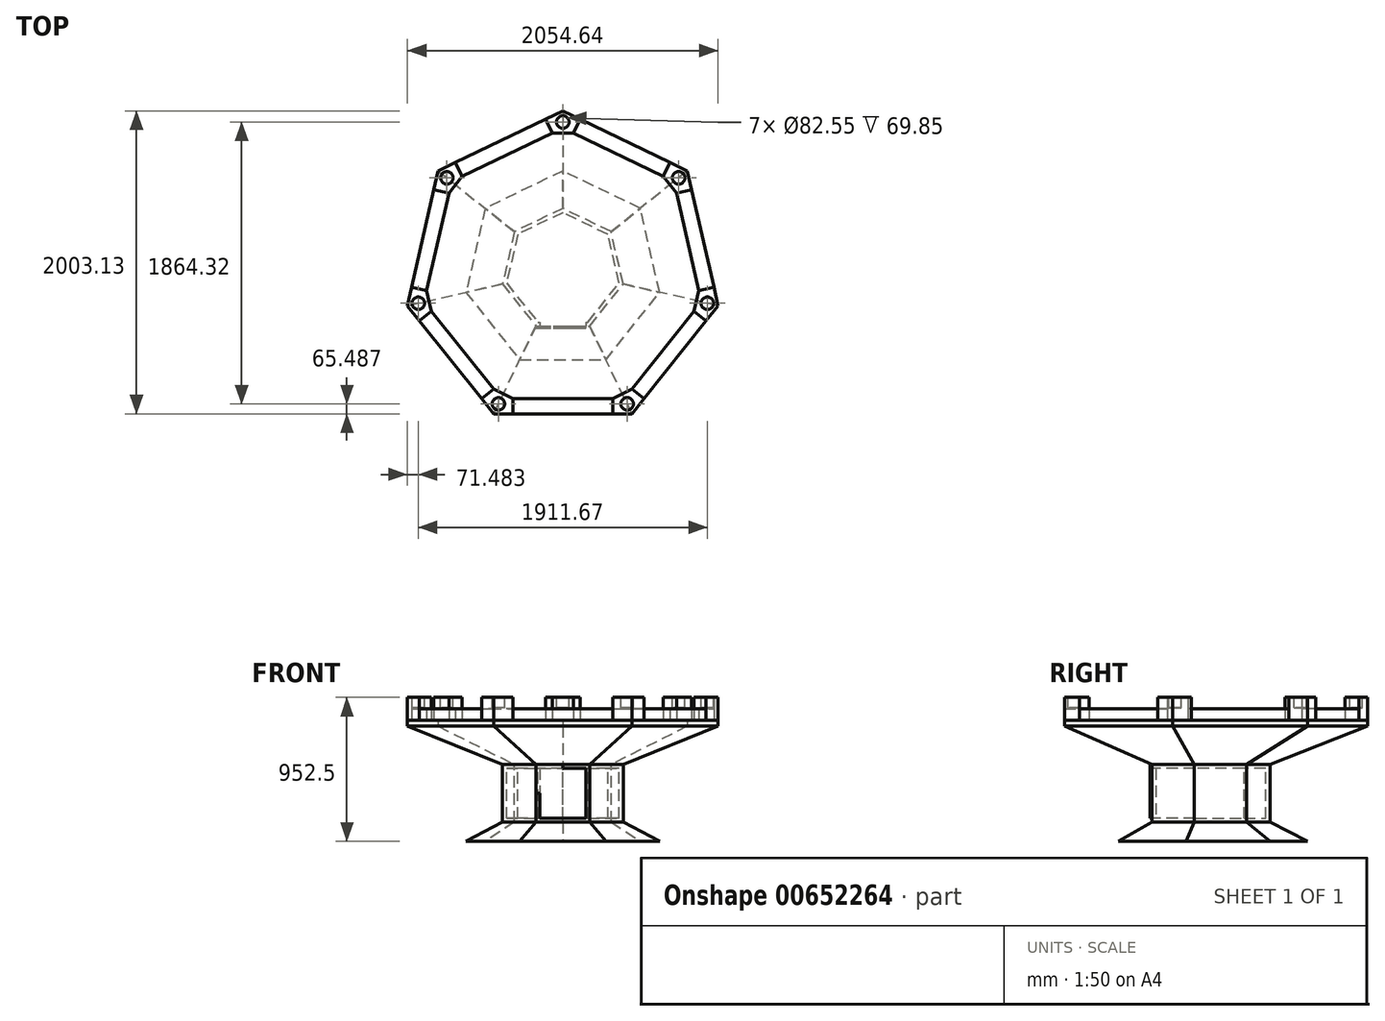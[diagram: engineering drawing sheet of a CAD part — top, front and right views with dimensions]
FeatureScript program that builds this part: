
annotation { "Feature Type Name" : "Feature", "Feature Type Description" : "" }
export const myFeature = defineFeature(function(context is Context, id is Id, definition is map)
    precondition{}
    {
        {
            var Q0;
            Q0=qCreatedBy(makeId("Top.planeOp"),FACE);
            var sketch = newSketch(context, id + "F0", { "sketchPlane" : qUnion([Q0])});
            skCircle(sketch, "E0.cCircle", {"center": v(0, 0) * mm, "radius": 949.39 * mm, "construction": true});
            skLineSegment(sketch, "E0.0", {"start": v(457.2, -949.39) * mm, "end": v(-457.2, -949.39) * mm});
            skLineSegment(sketch, "E0.1", {"start": v(-457.2, -949.39) * mm, "end": v(-1027.32, -234.48) * mm});
            skLineSegment(sketch, "E0.2", {"start": v(-1027.32, -234.48) * mm, "end": v(-823.85, 657) * mm});
            skLineSegment(sketch, "E0.3", {"start": v(-823.85, 657) * mm, "end": v(0, 1053.74) * mm});
            skLineSegment(sketch, "E0.4", {"start": v(0, 1053.74) * mm, "end": v(823.85, 657) * mm});
            skLineSegment(sketch, "E0.5", {"start": v(823.85, 657) * mm, "end": v(1027.32, -234.48) * mm});
            skLineSegment(sketch, "E0.6", {"start": v(1027.32, -234.48) * mm, "end": v(457.2, -949.39) * mm});
            skPoint(sketch, "E0.0.midPoint", {"position": v(0, -949.39) * mm});
            skSolve(sketch);
        }
        {
            var Q0;
            Q0 = qSketchRegion(id + "F0", true);
            extrude(context, id + "F1", {"entities" : qUnion([Q0]), "depth" : 38.1 * mm, "offsetDistance" : 25.4 * mm});
        }
        {
            var Q0;
            Q0=qCreatedBy(makeId("Front.planeOp"),FACE);
            var sketch = newSketch(context, id + "F2", { "sketchPlane" : qUnion([Q0])});
            skLineSegment(sketch, "E1.bottom", {"start": v(-2163.19, 801.55) * mm, "end": v(-1858.39, 801.55) * mm});
            skLineSegment(sketch, "E1.top", {"start": v(-2163.19, -1027.25) * mm, "end": v(-1858.39, -1027.25) * mm});
            skLineSegment(sketch, "E1.left", {"start": v(-2163.19, 801.55) * mm, "end": v(-2163.19, -1027.25) * mm});
            skLineSegment(sketch, "E1.right", {"start": v(-1858.39, 801.55) * mm, "end": v(-1858.39, -1027.25) * mm});
            skSolve(sketch);
        }
        {
            var Q0;
            Q0=makeQuery(id+"F1.opExtrude","CAP_FACE",FACE,{"disambiguationData":[OSD([sQuery(id+"F0.wireOp",EDGE,"E0.0"),sQuery(id+"F0.wireOp",EDGE,"E0.1"),sQuery(id+"F0.wireOp",EDGE,"E0.2"),sQuery(id+"F0.wireOp",EDGE,"E0.3"),sQuery(id+"F0.wireOp",EDGE,"E0.4"),sQuery(id+"F0.wireOp",EDGE,"E0.5"),sQuery(id+"F0.wireOp",EDGE,"E0.6")])],"isStart":false});
            var sketch = newSketch(context, id + "F3", { "sketchPlane" : qUnion([Q0])});
            skLineSegment(sketch, "E2", {"start": v(330.2, -949.39) * mm, "end": v(330.2, -847.79) * mm});
            skLineSegment(sketch, "E3", {"start": v(457.2, -949.39) * mm, "end": v(330.2, -949.39) * mm});
            skLineSegment(sketch, "E4", {"start": v(457.2, -949.39) * mm, "end": v(536.38, -850.1) * mm});
            skLineSegment(sketch, "E5", {"start": v(536.38, -850.1) * mm, "end": v(456.95, -786.75) * mm});
            skLineSegment(sketch, "E6", {"start": v(456.95, -786.75) * mm, "end": v(330.2, -847.79) * mm});
            skLineSegment(sketch, "E7", {"start": v(457.2, -949.39) * mm, "end": v(393.57, -817.27) * mm});
            skLineSegment(sketch, "E8", {"start": v(-457.2, -949.39) * mm, "end": v(-330.2, -949.39) * mm});
            skLineSegment(sketch, "E9", {"start": v(-457.2, -949.39) * mm, "end": v(-536.38, -850.1) * mm});
            skLineSegment(sketch, "E10", {"start": v(-536.38, -850.1) * mm, "end": v(-456.95, -786.75) * mm});
            skLineSegment(sketch, "E11", {"start": v(-330.2, -949.39) * mm, "end": v(-330.2, -847.79) * mm});
            skLineSegment(sketch, "E12", {"start": v(-456.95, -786.75) * mm, "end": v(-330.2, -847.79) * mm});
            skLineSegment(sketch, "E13", {"start": v(-457.2, -949.39) * mm, "end": v(-393.57, -817.27) * mm});
            skLineSegment(sketch, "E14", {"start": v(1027.32, -234.48) * mm, "end": v(948.14, -333.77) * mm});
            skLineSegment(sketch, "E15", {"start": v(1027.32, -234.48) * mm, "end": v(999.06, -110.66) * mm});
            skLineSegment(sketch, "E16", {"start": v(948.14, -333.77) * mm, "end": v(868.7, -270.42) * mm});
            skLineSegment(sketch, "E17", {"start": v(999.06, -110.66) * mm, "end": v(900, -133.27) * mm});
            skLineSegment(sketch, "E18", {"start": v(900, -133.27) * mm, "end": v(868.7, -270.42) * mm});
            skLineSegment(sketch, "E19", {"start": v(1027.32, -234.48) * mm, "end": v(884.35, -201.85) * mm});
            skLineSegment(sketch, "E20", {"start": v(-1027.32, -234.48) * mm, "end": v(-999.06, -110.66) * mm});
            skLineSegment(sketch, "E21", {"start": v(-1027.32, -234.48) * mm, "end": v(-948.14, -333.77) * mm});
            skLineSegment(sketch, "E22", {"start": v(-999.06, -110.66) * mm, "end": v(-900, -133.27) * mm});
            skLineSegment(sketch, "E23", {"start": v(-948.14, -333.77) * mm, "end": v(-868.7, -270.42) * mm});
            skLineSegment(sketch, "E24", {"start": v(-900, -133.27) * mm, "end": v(-868.7, -270.42) * mm});
            skLineSegment(sketch, "E25", {"start": v(-1027.32, -234.48) * mm, "end": v(-884.35, -201.85) * mm});
            skLineSegment(sketch, "E26", {"start": v(-823.85, 657) * mm, "end": v(-852.1, 533.18) * mm});
            skLineSegment(sketch, "E27", {"start": v(-823.85, 657) * mm, "end": v(-709.42, 712.1) * mm});
            skLineSegment(sketch, "E28", {"start": v(-709.42, 712.1) * mm, "end": v(-665.34, 620.56) * mm});
            skLineSegment(sketch, "E29", {"start": v(-852.1, 533.18) * mm, "end": v(-753.05, 510.57) * mm});
            skLineSegment(sketch, "E30", {"start": v(-753.05, 510.57) * mm, "end": v(-665.34, 620.56) * mm});
            skLineSegment(sketch, "E31", {"start": v(-823.85, 657) * mm, "end": v(-709.2, 565.57) * mm});
            skLineSegment(sketch, "E32", {"start": v(823.85, 657) * mm, "end": v(709.42, 712.1) * mm});
            skLineSegment(sketch, "E33", {"start": v(823.85, 657) * mm, "end": v(852.1, 533.18) * mm});
            skLineSegment(sketch, "E34", {"start": v(709.42, 712.1) * mm, "end": v(665.34, 620.56) * mm});
            skLineSegment(sketch, "E35", {"start": v(852.1, 533.18) * mm, "end": v(753.05, 510.57) * mm});
            skLineSegment(sketch, "E36", {"start": v(753.05, 510.57) * mm, "end": v(665.34, 620.56) * mm});
            skLineSegment(sketch, "E37", {"start": v(823.85, 657) * mm, "end": v(709.2, 565.57) * mm});
            skLineSegment(sketch, "E38", {"start": v(0, 1053.74) * mm, "end": v(-114.42, 998.64) * mm});
            skLineSegment(sketch, "E39", {"start": v(-114.42, 998.64) * mm, "end": v(-70.34, 907.1) * mm});
            skLineSegment(sketch, "E40", {"start": v(0, 1053.74) * mm, "end": v(114.42, 998.64) * mm});
            skLineSegment(sketch, "E41", {"start": v(114.42, 998.64) * mm, "end": v(70.34, 907.1) * mm});
            skLineSegment(sketch, "E42", {"start": v(70.34, 907.1) * mm, "end": v(-70.34, 907.1) * mm});
            skLineSegment(sketch, "E43", {"start": v(0, 1053.74) * mm, "end": v(0, 907.1) * mm});
            skLineSegment(sketch, "E44", {"start": v(-330.2, -847.79) * mm, "end": v(330.2, -847.79) * mm});
            skLineSegment(sketch, "E45", {"start": v(-330.2, -949.39) * mm, "end": v(330.2, -949.39) * mm});
            skLineSegment(sketch, "E46", {"start": v(868.7, -270.42) * mm, "end": v(456.95, -786.75) * mm});
            skLineSegment(sketch, "E47", {"start": v(948.14, -333.77) * mm, "end": v(536.38, -850.1) * mm});
            skLineSegment(sketch, "E48", {"start": v(852.1, 533.18) * mm, "end": v(999.06, -110.66) * mm});
            skLineSegment(sketch, "E49", {"start": v(753.05, 510.57) * mm, "end": v(900, -133.27) * mm});
            skLineSegment(sketch, "E50", {"start": v(114.42, 998.64) * mm, "end": v(709.42, 712.1) * mm});
            skLineSegment(sketch, "E51", {"start": v(70.34, 907.1) * mm, "end": v(665.34, 620.56) * mm});
            skLineSegment(sketch, "E52", {"start": v(-114.42, 998.64) * mm, "end": v(-709.42, 712.1) * mm});
            skLineSegment(sketch, "E53", {"start": v(-70.34, 907.1) * mm, "end": v(-665.34, 620.56) * mm});
            skLineSegment(sketch, "E54", {"start": v(-753.05, 510.57) * mm, "end": v(-900, -133.27) * mm});
            skLineSegment(sketch, "E55", {"start": v(-852.1, 533.18) * mm, "end": v(-999.06, -110.66) * mm});
            skLineSegment(sketch, "E56", {"start": v(-868.7, -270.42) * mm, "end": v(-456.95, -786.75) * mm});
            skLineSegment(sketch, "E57", {"start": v(-948.14, -333.77) * mm, "end": v(-536.38, -850.1) * mm});
            skLineSegment(sketch, "E58", {"start": v(-709.2, 565.57) * mm, "end": v(709.2, 565.57) * mm});
            skLineSegment(sketch, "E59", {"start": v(-393.57, -817.27) * mm, "end": v(-709.2, 565.57) * mm});
            skLineSegment(sketch, "E60", {"start": v(393.57, -817.27) * mm, "end": v(-884.35, -201.85) * mm});
            skLineSegment(sketch, "E61", {"start": v(884.35, -201.85) * mm, "end": v(-393.57, -817.27) * mm});
            skLineSegment(sketch, "E62", {"start": v(884.35, -201.85) * mm, "end": v(0, 907.1) * mm});
            skLineSegment(sketch, "E63", {"start": v(709.2, 565.57) * mm, "end": v(393.57, -817.27) * mm});
            skLineSegment(sketch, "E64", {"start": v(-884.35, -201.85) * mm, "end": v(0, 907.1) * mm});
            skPoint(sketch, "E65", {"position": v(-612, 139.68) * mm});
            skPoint(sketch, "E66", {"position": v(-490.78, -391.38) * mm});
            skPoint(sketch, "E67", {"position": v(490.78, -391.38) * mm});
            skPoint(sketch, "E68", {"position": v(612, 139.68) * mm});
            skPoint(sketch, "E69", {"position": v(-272.36, 565.57) * mm});
            skPoint(sketch, "E70", {"position": v(272.36, 565.57) * mm});
            skPoint(sketch, "E71", {"position": v(0, -627.73) * mm});
            skLineSegment(sketch, "E72.0", {"start": v(0, -627.73) * mm, "end": v(-627.73, 0) * mm});
            skLineSegment(sketch, "E72.1", {"start": v(-627.73, 0) * mm, "end": v(0, 627.73) * mm});
            skLineSegment(sketch, "E72.2", {"start": v(0, 627.73) * mm, "end": v(627.73, 0) * mm});
            skLineSegment(sketch, "E72.3", {"start": v(627.73, 0) * mm, "end": v(0, -627.73) * mm});
            skPoint(sketch, "E73", {"position": v(-313.87, 313.87) * mm});
            skPoint(sketch, "E74", {"position": v(313.87, 313.87) * mm});
            skPoint(sketch, "E75", {"position": v(313.87, -313.87) * mm});
            skPoint(sketch, "E76", {"position": v(-313.87, -313.87) * mm});
            skLineSegment(sketch, "E77.bottom", {"start": v(-313.87, 313.87) * mm, "end": v(313.87, 313.87) * mm});
            skLineSegment(sketch, "E77.top", {"start": v(-313.87, -313.87) * mm, "end": v(313.87, -313.87) * mm});
            skLineSegment(sketch, "E77.left", {"start": v(-313.87, 313.87) * mm, "end": v(-313.87, -313.87) * mm});
            skLineSegment(sketch, "E77.right", {"start": v(313.87, 313.87) * mm, "end": v(313.87, -313.87) * mm});
            skPoint(sketch, "E78", {"position": v(-313.87, 0) * mm});
            skPoint(sketch, "E79", {"position": v(0, 313.87) * mm});
            skPoint(sketch, "E80", {"position": v(313.87, 0) * mm});
            skPoint(sketch, "E81", {"position": v(0, -313.87) * mm});
            skLineSegment(sketch, "E82", {"start": v(-313.87, 0) * mm, "end": v(-313.87, 313.87) * mm});
            skLineSegment(sketch, "E83", {"start": v(-313.87, 0) * mm, "end": v(-313.87, -313.87) * mm});
            skLineSegment(sketch, "E84", {"start": v(313.87, -313.87) * mm, "end": v(313.87, 0) * mm});
            skLineSegment(sketch, "E85", {"start": v(313.87, 0) * mm, "end": v(313.87, 313.87) * mm});
            skPoint(sketch, "E86", {"position": v(-313.87, 156.93) * mm});
            skPoint(sketch, "E87", {"position": v(-313.87, -156.93) * mm});
            skPoint(sketch, "E88", {"position": v(313.87, -156.93) * mm});
            skPoint(sketch, "E89", {"position": v(313.87, 156.93) * mm});
            skSolve(sketch);
        }
        {
            var Q0;
            {var subQ0=sQuery(id+"F3.wireOp",EDGE,"E2");Q0=makeQuery(id+"F3.imprint","IMPRINT",FACE,{"disambiguationData":[TD([[makeQuery(id+"F3.imprint","IMPRINT",EDGE,{"derivedFrom":subQ0}),-1.0]])]});}
            var Q1;
            Q1=makeQuery(id+"F3.imprint","IMPRINT",FACE,{"disambiguationData":[TD([[makeQuery(id+"F3.imprint","IMPRINT",EDGE,{"derivedFrom":sQuery(id+"F3.wireOp",EDGE,"E4")}),-1.0]])]});
            extrude(context, id + "F4", {"entities" : qUnion([Q0, Q1]), "depth" : 152.4 * mm, "offsetDistance" : 25.4 * mm});
        }
        {
            var Q0;
            Q0=makeQuery(id+"F3.imprint","IMPRINT",FACE,{"disambiguationData":[TD([[makeQuery(id+"F3.imprint","IMPRINT",EDGE,{"derivedFrom":sQuery(id+"F3.wireOp",EDGE,"E9")}),-1.0]])]});
            var Q1;
            Q1=makeQuery(id+"F3.imprint","IMPRINT",FACE,{"disambiguationData":[TD([[makeQuery(id+"F3.imprint","IMPRINT",EDGE,{"derivedFrom":sQuery(id+"F3.wireOp",EDGE,"E8")}),-1.0]])]});
            extrude(context, id + "F5", {"entities" : qUnion([Q0, Q1]), "depth" : 152.4 * mm, "offsetDistance" : 25.4 * mm});
        }
        {
            var Q0;
            Q0=makeQuery(id+"F3.imprint","IMPRINT",FACE,{"disambiguationData":[TD([[makeQuery(id+"F3.imprint","IMPRINT",EDGE,{"derivedFrom":sQuery(id+"F3.wireOp",EDGE,"E15")}),-1.0]])]});
            var Q1;
            Q1=makeQuery(id+"F3.imprint","IMPRINT",FACE,{"disambiguationData":[TD([[makeQuery(id+"F3.imprint","IMPRINT",EDGE,{"derivedFrom":sQuery(id+"F3.wireOp",EDGE,"E14")}),-1.0]])]});
            extrude(context, id + "F6", {"entities" : qUnion([Q0, Q1]), "depth" : 152.4 * mm, "offsetDistance" : 25.4 * mm});
        }
        {
            var Q0;
            Q0=makeQuery(id+"F3.imprint","IMPRINT",FACE,{"disambiguationData":[TD([[makeQuery(id+"F3.imprint","IMPRINT",EDGE,{"derivedFrom":sQuery(id+"F3.wireOp",EDGE,"E20")}),-1.0]])]});
            var Q1;
            Q1=makeQuery(id+"F3.imprint","IMPRINT",FACE,{"disambiguationData":[TD([[makeQuery(id+"F3.imprint","IMPRINT",EDGE,{"derivedFrom":sQuery(id+"F3.wireOp",EDGE,"E21")}),-1.0]])]});
            extrude(context, id + "F7", {"entities" : qUnion([Q0, Q1]), "depth" : 152.4 * mm, "offsetDistance" : 25.4 * mm});
        }
        {
            var Q0;
            Q0=makeQuery(id+"F3.imprint","IMPRINT",FACE,{"disambiguationData":[TD([[makeQuery(id+"F3.imprint","IMPRINT",EDGE,{"derivedFrom":sQuery(id+"F3.wireOp",EDGE,"E27")}),-1.0]])]});
            var Q1;
            Q1=makeQuery(id+"F3.imprint","IMPRINT",FACE,{"disambiguationData":[TD([[makeQuery(id+"F3.imprint","IMPRINT",EDGE,{"derivedFrom":sQuery(id+"F3.wireOp",EDGE,"E26")}),-1.0]])]});
            extrude(context, id + "F8", {"entities" : qUnion([Q0, Q1]), "depth" : 152.4 * mm, "offsetDistance" : 25.4 * mm});
        }
        {
            var Q0;
            Q0=makeQuery(id+"F3.imprint","IMPRINT",FACE,{"disambiguationData":[TD([[makeQuery(id+"F3.imprint","IMPRINT",EDGE,{"derivedFrom":sQuery(id+"F3.wireOp",EDGE,"E32")}),-1.0]])]});
            var Q1;
            Q1=makeQuery(id+"F3.imprint","IMPRINT",FACE,{"disambiguationData":[TD([[makeQuery(id+"F3.imprint","IMPRINT",EDGE,{"derivedFrom":sQuery(id+"F3.wireOp",EDGE,"E33")}),-1.0]])]});
            var Q2;
            Q2=sQuery(id+"F3.wireOp",EDGE,"E34");
            var Q3;
            Q3=sQuery(id+"F3.wireOp",EDGE,"E32");
            var Q4;
            Q4=sQuery(id+"F3.wireOp",EDGE,"E35");
            var Q5;
            Q5=sQuery(id+"F3.wireOp",EDGE,"E33");
            var Q6;
            Q6=sQuery(id+"F3.wireOp",EDGE,"E36");
            var Q7;
            Q7=sQuery(id+"F3.wireOp",EDGE,"E37");
            extrude(context, id + "F9", {"entities" : qUnion([Q0, Q1]), "surfaceEntities" : qUnion([Q2, Q3, Q4, Q5, Q6, Q7]), "depth" : 152.4 * mm, "offsetDistance" : 25.4 * mm});
        }
        {
            var Q0;
            Q0=makeQuery(id+"F3.imprint","IMPRINT",FACE,{"disambiguationData":[TD([[makeQuery(id+"F3.imprint","IMPRINT",EDGE,{"derivedFrom":sQuery(id+"F3.wireOp",EDGE,"E38")}),-1.0]])]});
            var Q1;
            Q1=makeQuery(id+"F3.imprint","IMPRINT",FACE,{"disambiguationData":[TD([[makeQuery(id+"F3.imprint","IMPRINT",EDGE,{"derivedFrom":sQuery(id+"F3.wireOp",EDGE,"E40")}),-1.0]])]});
            extrude(context, id + "F10", {"entities" : qUnion([Q0, Q1]), "depth" : 152.4 * mm, "offsetDistance" : 25.4 * mm});
        }
        {
            var Q0;
            Q0=makeQuery(id+"F3.imprint","IMPRINT",FACE,{"disambiguationData":[TD([[makeQuery(id+"F3.imprint","IMPRINT",EDGE,{"derivedFrom":sQuery(id+"F3.wireOp",EDGE,"E28")}),1.0]])]});
            var Q1;
            Q1=makeQuery(id+"F3.imprint","IMPRINT",FACE,{"disambiguationData":[TD([[makeQuery(id+"F3.imprint","IMPRINT",EDGE,{"derivedFrom":sQuery(id+"F3.wireOp",EDGE,"E22")}),1.0]])]});
            var Q2;
            Q2=makeQuery(id+"F3.imprint","IMPRINT",FACE,{"disambiguationData":[TD([[makeQuery(id+"F3.imprint","IMPRINT",EDGE,{"derivedFrom":sQuery(id+"F3.wireOp",EDGE,"E10")}),1.0]])]});
            var Q3;
            Q3=makeQuery(id+"F3.imprint","IMPRINT",FACE,{"disambiguationData":[TD([[makeQuery(id+"F3.imprint","IMPRINT",EDGE,{"derivedFrom":sQuery(id+"F3.wireOp",EDGE,"E2")}),1.0]])]});
            var Q4;
            Q4=makeQuery(id+"F3.imprint","IMPRINT",FACE,{"disambiguationData":[TD([[makeQuery(id+"F3.imprint","IMPRINT",EDGE,{"derivedFrom":sQuery(id+"F3.wireOp",EDGE,"E5")}),-1.0]])]});
            var Q5;
            Q5=makeQuery(id+"F3.imprint","IMPRINT",FACE,{"disambiguationData":[TD([[makeQuery(id+"F3.imprint","IMPRINT",EDGE,{"derivedFrom":sQuery(id+"F3.wireOp",EDGE,"E17")}),-1.0]])]});
            var Q6;
            Q6=makeQuery(id+"F3.imprint","IMPRINT",FACE,{"disambiguationData":[TD([[makeQuery(id+"F3.imprint","IMPRINT",EDGE,{"derivedFrom":sQuery(id+"F3.wireOp",EDGE,"E34")}),-1.0]])]});
            extrude(context, id + "F11", {"entities" : qUnion([Q0, Q1, Q2, Q3, Q4, Q5, Q6]), "depth" : 76.2 * mm, "offsetDistance" : 25.4 * mm});
        }
        {
            var Q0;
            Q0=makeQuery(id+"F1.opExtrude","CAP_FACE",FACE,{"disambiguationData":[OSD([sQuery(id+"F0.wireOp",EDGE,"E0.0"),sQuery(id+"F0.wireOp",EDGE,"E0.1"),sQuery(id+"F0.wireOp",EDGE,"E0.2"),sQuery(id+"F0.wireOp",EDGE,"E0.3"),sQuery(id+"F0.wireOp",EDGE,"E0.4"),sQuery(id+"F0.wireOp",EDGE,"E0.5"),sQuery(id+"F0.wireOp",EDGE,"E0.6")])],"isStart":true});
            var sketch = newSketch(context, id + "F12", { "sketchPlane" : qUnion([Q0])});
            skLineSegment(sketch, "E90", {"start": v(-457.2, 949.39) * mm, "end": v(-1027.32, 234.48) * mm});
            skLineSegment(sketch, "E91", {"start": v(-1027.32, 234.48) * mm, "end": v(-823.85, -657) * mm});
            skLineSegment(sketch, "E92", {"start": v(-823.85, -657) * mm, "end": v(0, -1053.74) * mm});
            skLineSegment(sketch, "E93", {"start": v(0, -1053.74) * mm, "end": v(823.85, -657) * mm});
            skLineSegment(sketch, "E94", {"start": v(823.85, -657) * mm, "end": v(1027.32, 234.48) * mm});
            skLineSegment(sketch, "E95", {"start": v(1027.32, 234.48) * mm, "end": v(457.2, 949.39) * mm});
            skLineSegment(sketch, "E96", {"start": v(457.2, 949.39) * mm, "end": v(-457.2, 949.39) * mm});
            skSolve(sketch);
        }
        {
            var Q0;
            Q0=makeQuery(id+"F12.imprint","IMPRINT",FACE,{"disambiguationData":[TD([[makeQuery(id+"F12.imprint","IMPRINT",EDGE,{"derivedFrom":sQuery(id+"F12.wireOp",EDGE,"E91")}),1.0]])]});
            cPlane(context, id + "F13", {"entities" : qUnion([Q0]), "cplaneType" : CPlaneType.OFFSET, "offset" : 254 * mm, "width" : 152.4 * mm, "height" : 152.4 * mm});
        }
        {
            var Q0;
            Q0=qCreatedBy(id+"F13.planeOp",FACE);
            var sketch = newSketch(context, id + "F14", { "sketchPlane" : qUnion([Q0])});
            skCircle(sketch, "E97.cCircle", {"center": v(0, 0) * mm, "radius": 369.06 * mm, "construction": true});
            skLineSegment(sketch, "E97.0", {"start": v(-177.73, 369.06) * mm, "end": v(177.73, 369.06) * mm});
            skLineSegment(sketch, "E97.1", {"start": v(177.73, 369.06) * mm, "end": v(399.36, 91.15) * mm});
            skLineSegment(sketch, "E97.2", {"start": v(399.36, 91.15) * mm, "end": v(320.26, -255.4) * mm});
            skLineSegment(sketch, "E97.3", {"start": v(320.26, -255.4) * mm, "end": v(0, -409.63) * mm});
            skLineSegment(sketch, "E97.4", {"start": v(0, -409.63) * mm, "end": v(-320.26, -255.4) * mm});
            skLineSegment(sketch, "E97.5", {"start": v(-320.26, -255.4) * mm, "end": v(-399.36, 91.15) * mm});
            skLineSegment(sketch, "E97.6", {"start": v(-399.36, 91.15) * mm, "end": v(-177.73, 369.06) * mm});
            skPoint(sketch, "E97.0.midPoint", {"position": v(0, 369.06) * mm});
            skSolve(sketch);
        }
        {
            var Q0;
            Q0=qCreatedBy(id+"F13.planeOp",FACE);
            cPlane(context, id + "F15", {"entities" : qUnion([Q0]), "cplaneType" : CPlaneType.OFFSET, "offset" : 381 * mm, "width" : 152.4 * mm, "height" : 152.4 * mm});
        }
        {
            var Q0;
            Q0=qCreatedBy(id+"F15.planeOp",FACE);
            var sketch = newSketch(context, id + "F16", { "sketchPlane" : qUnion([Q0])});
            skLineSegment(sketch, "E98.0", {"start": v(-320.26, -255.4) * mm, "end": v(-399.36, 91.15) * mm});
            skLineSegment(sketch, "E98.1", {"start": v(-177.73, 369.06) * mm, "end": v(177.73, 369.06) * mm});
            skLineSegment(sketch, "E98.2", {"start": v(399.36, 91.15) * mm, "end": v(320.26, -255.4) * mm});
            skLineSegment(sketch, "E98.4", {"start": v(0, -409.63) * mm, "end": v(-320.26, -255.4) * mm});
            skLineSegment(sketch, "E98.5", {"start": v(-399.36, 91.15) * mm, "end": v(-177.73, 369.06) * mm});
            skLineSegment(sketch, "E98.6", {"start": v(177.73, 369.06) * mm, "end": v(399.36, 91.15) * mm});
            skLineSegment(sketch, "E98.7", {"start": v(320.26, -255.4) * mm, "end": v(0, -409.63) * mm});
            skSolve(sketch);
        }
        {
            var Q0;
            Q0=qCreatedBy(id+"F15.planeOp",FACE);
            cPlane(context, id + "F17", {"entities" : qUnion([Q0]), "cplaneType" : CPlaneType.OFFSET, "offset" : 127 * mm, "width" : 152.4 * mm, "height" : 152.4 * mm});
        }
        {
            var Q0;
            Q0=qCreatedBy(id+"F17.planeOp",FACE);
            var sketch = newSketch(context, id + "F18", { "sketchPlane" : qUnion([Q0])});
            skCircle(sketch, "E99.cCircle", {"center": v(0, 0) * mm, "radius": 949.39 * mm, "construction": true});
            skLineSegment(sketch, "E99.0", {"start": v(-457.2, 949.39) * mm, "end": v(457.2, 949.39) * mm});
            skLineSegment(sketch, "E99.1", {"start": v(457.2, 949.39) * mm, "end": v(1027.32, 234.48) * mm});
            skLineSegment(sketch, "E99.2", {"start": v(1027.32, 234.48) * mm, "end": v(823.85, -657) * mm});
            skLineSegment(sketch, "E99.3", {"start": v(823.85, -657) * mm, "end": v(0, -1053.74) * mm});
            skLineSegment(sketch, "E99.4", {"start": v(0, -1053.74) * mm, "end": v(-823.85, -657) * mm});
            skLineSegment(sketch, "E99.5", {"start": v(-823.85, -657) * mm, "end": v(-1027.32, 234.48) * mm});
            skLineSegment(sketch, "E99.6", {"start": v(-1027.32, 234.48) * mm, "end": v(-457.2, 949.39) * mm});
            skPoint(sketch, "E99.0.midPoint", {"position": v(0, 949.39) * mm});
            skCircle(sketch, "E100.cCircle", {"center": v(0, 0) * mm, "radius": 591.93 * mm, "construction": true});
            skPoint(sketch, "E100.cCircle.perimeterSnap0", {"position": v(742.26, 591.93) * mm});
            skLineSegment(sketch, "E100.0", {"start": v(-285.06, 591.93) * mm, "end": v(285.06, 591.93) * mm});
            skLineSegment(sketch, "E100.1", {"start": v(285.06, 591.93) * mm, "end": v(640.52, 146.2) * mm});
            skLineSegment(sketch, "E100.2", {"start": v(640.52, 146.2) * mm, "end": v(513.66, -409.63) * mm});
            skLineSegment(sketch, "E100.3", {"start": v(513.66, -409.63) * mm, "end": v(0, -657) * mm});
            skLineSegment(sketch, "E100.4", {"start": v(0, -657) * mm, "end": v(-513.66, -409.63) * mm});
            skLineSegment(sketch, "E100.5", {"start": v(-513.66, -409.63) * mm, "end": v(-640.52, 146.2) * mm});
            skLineSegment(sketch, "E100.6", {"start": v(-640.52, 146.2) * mm, "end": v(-285.06, 591.93) * mm});
            skPoint(sketch, "E100.0.midPoint", {"position": v(0, 591.93) * mm});
            skPoint(sketch, "E100.0.midPoint.positionSnap0", {"position": v(742.26, 591.93) * mm});
            skSolve(sketch);
        }
        {
            var Q1;
            Q1=makeQuery(id+"F12.imprint","IMPRINT",FACE,{"disambiguationData":[TD([[makeQuery(id+"F12.imprint","IMPRINT",EDGE,{"derivedFrom":sQuery(id+"F12.wireOp",EDGE,"E91")}),1.0]])]});
            var Q2;
            Q2=makeQuery(id+"F14.imprint","IMPRINT",FACE,{"disambiguationData":[TD([[makeQuery(id+"F14.imprint","IMPRINT",EDGE,{"derivedFrom":sQuery(id+"F14.wireOp",EDGE,"E97.0")}),-1.0]])]});
            loft(context, id + "F19", {"sheetProfilesArray" : [{ "sheetProfileEntities" : qUnion([Q1]) }, { "sheetProfileEntities" : qUnion([Q2]) }]});
        }
        {
            var Q0;
            Q0=makeQuery(id+"F16.imprint","IMPRINT",FACE,{"disambiguationData":[TD([[makeQuery(id+"F16.imprint","IMPRINT",EDGE,{"derivedFrom":sQuery(id+"F16.wireOp",EDGE,"E98.0")}),-1.0]])]});
            var Q1;
            Q1=makeQuery(id+"F18.imprint","IMPRINT",FACE,{"disambiguationData":[TD([[makeQuery(id+"F18.imprint","IMPRINT",EDGE,{"derivedFrom":sQuery(id+"F18.wireOp",EDGE,"E100.0")}),-1.0]])]});
            loft(context, id + "F20", {"sheetProfilesArray" : [{ "sheetProfileEntities" : qUnion([Q0]) }, { "sheetProfileEntities" : qUnion([Q1]) }]});
        }
        {
            var Q0;
            Q0=makeQuery(id+"F7.opExtrude","CAP_FACE",FACE,{"disambiguationData":[OSD([sQuery(id+"F3.wireOp",EDGE,"E20"),sQuery(id+"F3.wireOp",EDGE,"E21"),sQuery(id+"F3.wireOp",EDGE,"E22"),sQuery(id+"F3.wireOp",EDGE,"E23"),sQuery(id+"F3.wireOp",EDGE,"E24")])],"isStart":false});
            var sketch = newSketch(context, id + "F21", { "sketchPlane" : qUnion([Q0])});
            skLineSegment(sketch, "E101", {"start": v(-1027.32, -234.48) * mm, "end": v(-884.35, -201.85) * mm});
            skLineSegment(sketch, "E102", {"start": v(-949.53, -121.97) * mm, "end": v(-955.84, -218.16) * mm});
            skLineSegment(sketch, "E103", {"start": v(-908.42, -302.1) * mm, "end": v(-955.84, -218.16) * mm});
            skCircle(sketch, "E104", {"center": v(-955.84, -218.16) * mm, "radius": 41.28 * mm});
            skSolve(sketch);
        }
        {
            var Q0;
            Q0 = qSketchRegion(id + "F21", true);
            extrude(context, id + "F22", {"entities" : qUnion([Q0]), "operationType" : NewBodyOperationType.REMOVE, "oppositeDirection" : true, "depth" : 69.85 * mm, "offsetDistance" : 25.4 * mm});
        }
        {
            var Q0;
            Q0=makeQuery(id+"F5.opExtrude","CAP_FACE",FACE,{"disambiguationData":[OSD([sQuery(id+"F3.wireOp",EDGE,"E8"),sQuery(id+"F3.wireOp",EDGE,"E9"),sQuery(id+"F3.wireOp",EDGE,"E10"),sQuery(id+"F3.wireOp",EDGE,"E11"),sQuery(id+"F3.wireOp",EDGE,"E12")])],"isStart":false});
            var sketch = newSketch(context, id + "F23", { "sketchPlane" : qUnion([Q0])});
            skLineSegment(sketch, "E105", {"start": v(-457.2, -949.39) * mm, "end": v(-394.13, -818.42) * mm});
            skPoint(sketch, "E105.endSnap0", {"position": v(-496.67, -818.42) * mm});
            skLineSegment(sketch, "E106", {"start": v(-496.67, -818.42) * mm, "end": v(-425.67, -883.9) * mm});
            skLineSegment(sketch, "E107", {"start": v(-425.67, -883.9) * mm, "end": v(-330.2, -898.59) * mm});
            skCircle(sketch, "E108", {"center": v(-425.67, -883.9) * mm, "radius": 41.28 * mm});
            skSolve(sketch);
        }
        {
            var Q0;
            {var subQ1=sQuery(id+"F23.wireOp",EDGE,"E105");var subQ3=sQuery(id+"F23.wireOp",EDGE,"E108");var subQ4=makeQuery(id+"F23.imprint","INTERSECT",VERTEX,{"disambiguationData":[OD(1.0)],"derivedFrom":[subQ1,subQ3]});Q0=makeQuery(id+"F23.imprint","IMPRINT",FACE,{"disambiguationData":[TD([[makeQuery(id+"F23.imprint","IMPRINT",EDGE,{"disambiguationData":[TD([[subQ4,1.0]])],"derivedFrom":subQ3}),1.0]])]});}
            var Q1;
            {var subQ1=sQuery(id+"F23.wireOp",EDGE,"E105");var subQ3=sQuery(id+"F23.wireOp",EDGE,"E108");var subQ4=makeQuery(id+"F23.imprint","INTERSECT",VERTEX,{"disambiguationData":[OD(0.0)],"derivedFrom":[subQ1,subQ3]});Q1=makeQuery(id+"F23.imprint","IMPRINT",FACE,{"disambiguationData":[TD([[makeQuery(id+"F23.imprint","IMPRINT",EDGE,{"disambiguationData":[TD([[subQ4,-1.0]])],"derivedFrom":subQ3}),1.0]])]});}
            var Q2;
            {var subQ1=sQuery(id+"F23.wireOp",EDGE,"E105");var subQ3=sQuery(id+"F23.wireOp",EDGE,"E108");var subQ4=makeQuery(id+"F23.imprint","INTERSECT",VERTEX,{"disambiguationData":[OD(0.0)],"derivedFrom":[subQ1,subQ3]});Q2=makeQuery(id+"F23.imprint","IMPRINT",FACE,{"disambiguationData":[TD([[makeQuery(id+"F23.imprint","IMPRINT",EDGE,{"disambiguationData":[TD([[subQ4,1.0]])],"derivedFrom":subQ3}),1.0]])]});}
            var Q3;
            {var subQ1=sQuery(id+"F23.wireOp",EDGE,"E105");var subQ3=sQuery(id+"F23.wireOp",EDGE,"E108");var subQ4=makeQuery(id+"F23.imprint","INTERSECT",VERTEX,{"disambiguationData":[OD(1.0)],"derivedFrom":[subQ1,subQ3]});Q3=makeQuery(id+"F23.imprint","IMPRINT",FACE,{"disambiguationData":[TD([[makeQuery(id+"F23.imprint","IMPRINT",EDGE,{"disambiguationData":[TD([[subQ4,-1.0]])],"derivedFrom":subQ3}),1.0]])]});}
            extrude(context, id + "F24", {"entities" : qUnion([Q0, Q1, Q2, Q3]), "operationType" : NewBodyOperationType.REMOVE, "oppositeDirection" : true, "depth" : 69.85 * mm, "offsetDistance" : 25.4 * mm});
        }
        {
            var Q0;
            Q0=makeQuery(id+"F4.opExtrude","CAP_FACE",FACE,{"disambiguationData":[OSD([sQuery(id+"F3.wireOp",EDGE,"E2"),sQuery(id+"F3.wireOp",EDGE,"E3"),sQuery(id+"F3.wireOp",EDGE,"E4"),sQuery(id+"F3.wireOp",EDGE,"E5"),sQuery(id+"F3.wireOp",EDGE,"E6")])],"isStart":false});
            var sketch = newSketch(context, id + "F25", { "sketchPlane" : qUnion([Q0])});
            skLineSegment(sketch, "E109", {"start": v(393.57, -817.27) * mm, "end": v(457.2, -949.39) * mm});
            skLineSegment(sketch, "E110", {"start": v(330.2, -898.59) * mm, "end": v(425.39, -883.33) * mm});
            skLineSegment(sketch, "E111", {"start": v(425.39, -883.33) * mm, "end": v(496.67, -818.42) * mm});
            skCircle(sketch, "E112", {"center": v(425.39, -883.33) * mm, "radius": 41.28 * mm});
            skSolve(sketch);
        }
        {
            var Q0;
            {var subQ1=sQuery(id+"F25.wireOp",EDGE,"E109");var subQ3=sQuery(id+"F25.wireOp",EDGE,"E112");var subQ4=makeQuery(id+"F25.imprint","INTERSECT",VERTEX,{"disambiguationData":[OD(1.0)],"derivedFrom":[subQ1,subQ3]});Q0=makeQuery(id+"F25.imprint","IMPRINT",FACE,{"disambiguationData":[TD([[makeQuery(id+"F25.imprint","IMPRINT",EDGE,{"disambiguationData":[TD([[subQ4,-1.0]])],"derivedFrom":subQ3}),1.0]])]});}
            var Q1;
            {var subQ1=sQuery(id+"F25.wireOp",EDGE,"E109");var subQ3=sQuery(id+"F25.wireOp",EDGE,"E112");var subQ4=makeQuery(id+"F25.imprint","INTERSECT",VERTEX,{"disambiguationData":[OD(1.0)],"derivedFrom":[subQ1,subQ3]});Q1=makeQuery(id+"F25.imprint","IMPRINT",FACE,{"disambiguationData":[TD([[makeQuery(id+"F25.imprint","IMPRINT",EDGE,{"disambiguationData":[TD([[subQ4,1.0]])],"derivedFrom":subQ3}),1.0]])]});}
            var Q2;
            {var subQ1=sQuery(id+"F25.wireOp",EDGE,"E109");var subQ3=sQuery(id+"F25.wireOp",EDGE,"E112");var subQ4=makeQuery(id+"F25.imprint","INTERSECT",VERTEX,{"disambiguationData":[OD(0.0)],"derivedFrom":[subQ1,subQ3]});Q2=makeQuery(id+"F25.imprint","IMPRINT",FACE,{"disambiguationData":[TD([[makeQuery(id+"F25.imprint","IMPRINT",EDGE,{"disambiguationData":[TD([[subQ4,1.0]])],"derivedFrom":subQ3}),1.0]])]});}
            var Q3;
            {var subQ1=sQuery(id+"F25.wireOp",EDGE,"E109");var subQ3=sQuery(id+"F25.wireOp",EDGE,"E112");var subQ4=makeQuery(id+"F25.imprint","INTERSECT",VERTEX,{"disambiguationData":[OD(0.0)],"derivedFrom":[subQ1,subQ3]});Q3=makeQuery(id+"F25.imprint","IMPRINT",FACE,{"disambiguationData":[TD([[makeQuery(id+"F25.imprint","IMPRINT",EDGE,{"disambiguationData":[TD([[subQ4,-1.0]])],"derivedFrom":subQ3}),1.0]])]});}
            extrude(context, id + "F26", {"entities" : qUnion([Q0, Q1, Q2, Q3]), "operationType" : NewBodyOperationType.REMOVE, "oppositeDirection" : true, "depth" : 69.85 * mm, "offsetDistance" : 25.4 * mm});
        }
        {
            var Q0;
            Q0=makeQuery(id+"F6.opExtrude","CAP_FACE",FACE,{"disambiguationData":[OSD([sQuery(id+"F3.wireOp",EDGE,"E14"),sQuery(id+"F3.wireOp",EDGE,"E15"),sQuery(id+"F3.wireOp",EDGE,"E16"),sQuery(id+"F3.wireOp",EDGE,"E17"),sQuery(id+"F3.wireOp",EDGE,"E18")])],"isStart":false});
            var sketch = newSketch(context, id + "F27", { "sketchPlane" : qUnion([Q0])});
            skLineSegment(sketch, "E113", {"start": v(884.35, -201.85) * mm, "end": v(1027.32, -234.48) * mm});
            skLineSegment(sketch, "E114", {"start": v(908.42, -302.1) * mm, "end": v(955.84, -218.16) * mm});
            skLineSegment(sketch, "E115", {"start": v(949.53, -121.97) * mm, "end": v(955.84, -218.16) * mm});
            skCircle(sketch, "E116", {"center": v(955.84, -218.16) * mm, "radius": 41.28 * mm});
            skSolve(sketch);
        }
        {
            var Q0;
            {var subQ1=sQuery(id+"F27.wireOp",EDGE,"E113");var subQ3=sQuery(id+"F27.wireOp",EDGE,"E116");var subQ4=makeQuery(id+"F27.imprint","INTERSECT",VERTEX,{"disambiguationData":[OD(0.0)],"derivedFrom":[subQ1,subQ3]});Q0=makeQuery(id+"F27.imprint","IMPRINT",FACE,{"disambiguationData":[TD([[makeQuery(id+"F27.imprint","IMPRINT",EDGE,{"disambiguationData":[TD([[subQ4,-1.0]])],"derivedFrom":subQ3}),1.0]])]});}
            var Q1;
            {var subQ1=sQuery(id+"F27.wireOp",EDGE,"E113");var subQ3=sQuery(id+"F27.wireOp",EDGE,"E116");var subQ4=makeQuery(id+"F27.imprint","INTERSECT",VERTEX,{"disambiguationData":[OD(1.0)],"derivedFrom":[subQ1,subQ3]});Q1=makeQuery(id+"F27.imprint","IMPRINT",FACE,{"disambiguationData":[TD([[makeQuery(id+"F27.imprint","IMPRINT",EDGE,{"disambiguationData":[TD([[subQ4,1.0]])],"derivedFrom":subQ3}),1.0]])]});}
            var Q2;
            {var subQ1=sQuery(id+"F27.wireOp",EDGE,"E113");var subQ3=sQuery(id+"F27.wireOp",EDGE,"E116");var subQ4=makeQuery(id+"F27.imprint","INTERSECT",VERTEX,{"disambiguationData":[OD(1.0)],"derivedFrom":[subQ1,subQ3]});Q2=makeQuery(id+"F27.imprint","IMPRINT",FACE,{"disambiguationData":[TD([[makeQuery(id+"F27.imprint","IMPRINT",EDGE,{"disambiguationData":[TD([[subQ4,-1.0]])],"derivedFrom":subQ3}),1.0]])]});}
            var Q3;
            {var subQ1=sQuery(id+"F27.wireOp",EDGE,"E113");var subQ3=sQuery(id+"F27.wireOp",EDGE,"E116");var subQ4=makeQuery(id+"F27.imprint","INTERSECT",VERTEX,{"disambiguationData":[OD(0.0)],"derivedFrom":[subQ1,subQ3]});Q3=makeQuery(id+"F27.imprint","IMPRINT",FACE,{"disambiguationData":[TD([[makeQuery(id+"F27.imprint","IMPRINT",EDGE,{"disambiguationData":[TD([[subQ4,1.0]])],"derivedFrom":subQ3}),1.0]])]});}
            extrude(context, id + "F28", {"entities" : qUnion([Q0, Q1, Q2, Q3]), "operationType" : NewBodyOperationType.REMOVE, "oppositeDirection" : true, "depth" : 69.85 * mm, "offsetDistance" : 25.4 * mm});
        }
        {
            var Q0;
            Q0=makeQuery(id+"F9.opExtrude","CAP_FACE",FACE,{"disambiguationData":[OSD([sQuery(id+"F3.wireOp",EDGE,"E32"),sQuery(id+"F3.wireOp",EDGE,"E33"),sQuery(id+"F3.wireOp",EDGE,"E34"),sQuery(id+"F3.wireOp",EDGE,"E35"),sQuery(id+"F3.wireOp",EDGE,"E36")])],"isStart":false});
            var sketch = newSketch(context, id + "F29", { "sketchPlane" : qUnion([Q0])});
            skLineSegment(sketch, "E117", {"start": v(709.2, 565.57) * mm, "end": v(823.85, 657) * mm});
            skLineSegment(sketch, "E118", {"start": v(802.58, 521.88) * mm, "end": v(766.52, 611.28) * mm});
            skLineSegment(sketch, "E119", {"start": v(687.38, 666.33) * mm, "end": v(766.52, 611.28) * mm});
            skCircle(sketch, "E120", {"center": v(766.52, 611.28) * mm, "radius": 41.28 * mm});
            skSolve(sketch);
        }
        {
            var Q0;
            {var subQ1=sQuery(id+"F29.wireOp",EDGE,"E117");var subQ3=sQuery(id+"F29.wireOp",EDGE,"E120");var subQ4=makeQuery(id+"F29.imprint","INTERSECT",VERTEX,{"disambiguationData":[OD(1.0)],"derivedFrom":[subQ1,subQ3]});Q0=makeQuery(id+"F29.imprint","IMPRINT",FACE,{"disambiguationData":[TD([[makeQuery(id+"F29.imprint","IMPRINT",EDGE,{"disambiguationData":[TD([[subQ4,-1.0]])],"derivedFrom":subQ3}),1.0]])]});}
            var Q1;
            {var subQ1=sQuery(id+"F29.wireOp",EDGE,"E117");var subQ3=sQuery(id+"F29.wireOp",EDGE,"E120");var subQ4=makeQuery(id+"F29.imprint","INTERSECT",VERTEX,{"disambiguationData":[OD(0.0)],"derivedFrom":[subQ1,subQ3]});Q1=makeQuery(id+"F29.imprint","IMPRINT",FACE,{"disambiguationData":[TD([[makeQuery(id+"F29.imprint","IMPRINT",EDGE,{"disambiguationData":[TD([[subQ4,1.0]])],"derivedFrom":subQ3}),1.0]])]});}
            var Q2;
            {var subQ1=sQuery(id+"F29.wireOp",EDGE,"E117");var subQ3=sQuery(id+"F29.wireOp",EDGE,"E120");var subQ4=makeQuery(id+"F29.imprint","INTERSECT",VERTEX,{"disambiguationData":[OD(0.0)],"derivedFrom":[subQ1,subQ3]});Q2=makeQuery(id+"F29.imprint","IMPRINT",FACE,{"disambiguationData":[TD([[makeQuery(id+"F29.imprint","IMPRINT",EDGE,{"disambiguationData":[TD([[subQ4,-1.0]])],"derivedFrom":subQ3}),1.0]])]});}
            var Q3;
            {var subQ1=sQuery(id+"F29.wireOp",EDGE,"E117");var subQ3=sQuery(id+"F29.wireOp",EDGE,"E120");var subQ4=makeQuery(id+"F29.imprint","INTERSECT",VERTEX,{"disambiguationData":[OD(1.0)],"derivedFrom":[subQ1,subQ3]});Q3=makeQuery(id+"F29.imprint","IMPRINT",FACE,{"disambiguationData":[TD([[makeQuery(id+"F29.imprint","IMPRINT",EDGE,{"disambiguationData":[TD([[subQ4,1.0]])],"derivedFrom":subQ3}),1.0]])]});}
            extrude(context, id + "F30", {"entities" : qUnion([Q0, Q1, Q2, Q3]), "operationType" : NewBodyOperationType.REMOVE, "oppositeDirection" : true, "depth" : 69.85 * mm, "offsetDistance" : 25.4 * mm});
        }
        {
            var Q0;
            Q0=makeQuery(id+"F10.opExtrude","CAP_FACE",FACE,{"disambiguationData":[OSD([sQuery(id+"F3.wireOp",EDGE,"E38"),sQuery(id+"F3.wireOp",EDGE,"E39"),sQuery(id+"F3.wireOp",EDGE,"E40"),sQuery(id+"F3.wireOp",EDGE,"E41"),sQuery(id+"F3.wireOp",EDGE,"E42")])],"isStart":false});
            var sketch = newSketch(context, id + "F31", { "sketchPlane" : qUnion([Q0])});
            skLineSegment(sketch, "E121", {"start": v(0, 907.1) * mm, "end": v(0, 1053.74) * mm});
            skLineSegment(sketch, "E122", {"start": v(92.38, 952.87) * mm, "end": v(0, 980.42) * mm});
            skLineSegment(sketch, "E123", {"start": v(-92.38, 952.87) * mm, "end": v(0, 980.42) * mm});
            skCircle(sketch, "E124", {"center": v(0, 980.42) * mm, "radius": 41.28 * mm});
            skSolve(sketch);
        }
        {
            var Q0;
            {var subQ1=sQuery(id+"F31.wireOp",EDGE,"E121");var subQ3=sQuery(id+"F31.wireOp",EDGE,"E124");var subQ4=makeQuery(id+"F31.imprint","INTERSECT",VERTEX,{"disambiguationData":[OD(1.0)],"derivedFrom":[subQ1,subQ3]});Q0=makeQuery(id+"F31.imprint","IMPRINT",FACE,{"disambiguationData":[TD([[makeQuery(id+"F31.imprint","IMPRINT",EDGE,{"disambiguationData":[TD([[subQ4,-1.0]])],"derivedFrom":subQ3}),1.0]])]});}
            var Q1;
            {var subQ1=sQuery(id+"F31.wireOp",EDGE,"E121");var subQ3=sQuery(id+"F31.wireOp",EDGE,"E124");var subQ4=makeQuery(id+"F31.imprint","INTERSECT",VERTEX,{"disambiguationData":[OD(0.0)],"derivedFrom":[subQ1,subQ3]});Q1=makeQuery(id+"F31.imprint","IMPRINT",FACE,{"disambiguationData":[TD([[makeQuery(id+"F31.imprint","IMPRINT",EDGE,{"disambiguationData":[TD([[subQ4,1.0]])],"derivedFrom":subQ3}),1.0]])]});}
            var Q2;
            {var subQ1=sQuery(id+"F31.wireOp",EDGE,"E121");var subQ3=sQuery(id+"F31.wireOp",EDGE,"E124");var subQ4=makeQuery(id+"F31.imprint","INTERSECT",VERTEX,{"disambiguationData":[OD(0.0)],"derivedFrom":[subQ1,subQ3]});Q2=makeQuery(id+"F31.imprint","IMPRINT",FACE,{"disambiguationData":[TD([[makeQuery(id+"F31.imprint","IMPRINT",EDGE,{"disambiguationData":[TD([[subQ4,-1.0]])],"derivedFrom":subQ3}),1.0]])]});}
            var Q3;
            {var subQ1=sQuery(id+"F31.wireOp",EDGE,"E121");var subQ3=sQuery(id+"F31.wireOp",EDGE,"E124");var subQ4=makeQuery(id+"F31.imprint","INTERSECT",VERTEX,{"disambiguationData":[OD(1.0)],"derivedFrom":[subQ1,subQ3]});Q3=makeQuery(id+"F31.imprint","IMPRINT",FACE,{"disambiguationData":[TD([[makeQuery(id+"F31.imprint","IMPRINT",EDGE,{"disambiguationData":[TD([[subQ4,1.0]])],"derivedFrom":subQ3}),1.0]])]});}
            extrude(context, id + "F32", {"entities" : qUnion([Q0, Q1, Q2, Q3]), "operationType" : NewBodyOperationType.REMOVE, "oppositeDirection" : true, "depth" : 69.85 * mm, "offsetDistance" : 25.4 * mm});
        }
        {
            var Q0;
            Q0=makeQuery(id+"F8.opExtrude","CAP_FACE",FACE,{"disambiguationData":[OSD([sQuery(id+"F3.wireOp",EDGE,"E26"),sQuery(id+"F3.wireOp",EDGE,"E27"),sQuery(id+"F3.wireOp",EDGE,"E28"),sQuery(id+"F3.wireOp",EDGE,"E29"),sQuery(id+"F3.wireOp",EDGE,"E30")])],"isStart":false});
            var sketch = newSketch(context, id + "F33", { "sketchPlane" : qUnion([Q0])});
            skLineSegment(sketch, "E125", {"start": v(-709.2, 565.57) * mm, "end": v(-823.85, 657) * mm});
            skLineSegment(sketch, "E126", {"start": v(-802.58, 521.88) * mm, "end": v(-766.52, 611.28) * mm});
            skLineSegment(sketch, "E127", {"start": v(-687.38, 666.33) * mm, "end": v(-766.52, 611.28) * mm});
            skCircle(sketch, "E128", {"center": v(-766.52, 611.28) * mm, "radius": 41.28 * mm});
            skSolve(sketch);
        }
        {
            var Q0;
            {var subQ1=sQuery(id+"F33.wireOp",EDGE,"E125");var subQ3=sQuery(id+"F33.wireOp",EDGE,"E128");var subQ4=makeQuery(id+"F33.imprint","INTERSECT",VERTEX,{"disambiguationData":[OD(1.0)],"derivedFrom":[subQ1,subQ3]});Q0=makeQuery(id+"F33.imprint","IMPRINT",FACE,{"disambiguationData":[TD([[makeQuery(id+"F33.imprint","IMPRINT",EDGE,{"disambiguationData":[TD([[subQ4,1.0]])],"derivedFrom":subQ3}),1.0]])]});}
            var Q1;
            {var subQ1=sQuery(id+"F33.wireOp",EDGE,"E125");var subQ3=sQuery(id+"F33.wireOp",EDGE,"E128");var subQ4=makeQuery(id+"F33.imprint","INTERSECT",VERTEX,{"disambiguationData":[OD(1.0)],"derivedFrom":[subQ1,subQ3]});Q1=makeQuery(id+"F33.imprint","IMPRINT",FACE,{"disambiguationData":[TD([[makeQuery(id+"F33.imprint","IMPRINT",EDGE,{"disambiguationData":[TD([[subQ4,-1.0]])],"derivedFrom":subQ3}),1.0]])]});}
            var Q2;
            {var subQ1=sQuery(id+"F33.wireOp",EDGE,"E125");var subQ3=sQuery(id+"F33.wireOp",EDGE,"E128");var subQ4=makeQuery(id+"F33.imprint","INTERSECT",VERTEX,{"disambiguationData":[OD(0.0)],"derivedFrom":[subQ1,subQ3]});Q2=makeQuery(id+"F33.imprint","IMPRINT",FACE,{"disambiguationData":[TD([[makeQuery(id+"F33.imprint","IMPRINT",EDGE,{"disambiguationData":[TD([[subQ4,1.0]])],"derivedFrom":subQ3}),1.0]])]});}
            var Q3;
            {var subQ1=sQuery(id+"F33.wireOp",EDGE,"E125");var subQ3=sQuery(id+"F33.wireOp",EDGE,"E128");var subQ4=makeQuery(id+"F33.imprint","INTERSECT",VERTEX,{"disambiguationData":[OD(0.0)],"derivedFrom":[subQ1,subQ3]});Q3=makeQuery(id+"F33.imprint","IMPRINT",FACE,{"disambiguationData":[TD([[makeQuery(id+"F33.imprint","IMPRINT",EDGE,{"disambiguationData":[TD([[subQ4,-1.0]])],"derivedFrom":subQ3}),1.0]])]});}
            extrude(context, id + "F34", {"entities" : qUnion([Q0, Q1, Q2, Q3]), "operationType" : NewBodyOperationType.REMOVE, "oppositeDirection" : true, "depth" : 69.85 * mm, "offsetDistance" : 25.4 * mm});
        }
        {
            var Q0;
            Q0=makeQuery(id+"F14.imprint","IMPRINT",FACE,{"disambiguationData":[TD([[makeQuery(id+"F14.imprint","IMPRINT",EDGE,{"derivedFrom":sQuery(id+"F14.wireOp",EDGE,"E97.0")}),-1.0]])]});
            extrude(context, id + "F35", {"entities" : qUnion([Q0]), "operationType" : NewBodyOperationType.ADD, "depth" : 25.4 * mm, "offsetDistance" : 25.4 * mm});
        }
        {
            var Q0;
            Q0=makeQuery(id+"F35.opExtrude","CAP_FACE",FACE,{"disambiguationData":[OSD([sQuery(id+"F14.wireOp",EDGE,"E97.0"),sQuery(id+"F14.wireOp",EDGE,"E97.1"),sQuery(id+"F14.wireOp",EDGE,"E97.2"),sQuery(id+"F14.wireOp",EDGE,"E97.3"),sQuery(id+"F14.wireOp",EDGE,"E97.4"),sQuery(id+"F14.wireOp",EDGE,"E97.5"),sQuery(id+"F14.wireOp",EDGE,"E97.6")])],"isStart":false});
            var sketch = newSketch(context, id + "F36", { "sketchPlane" : qUnion([Q0])});
            skLineSegment(sketch, "E129.0.0", {"start": v(-177.73, 369.06) * mm, "end": v(-399.36, 91.15) * mm});
            skLineSegment(sketch, "E129.0.1", {"start": v(-399.36, 91.15) * mm, "end": v(-320.26, -255.4) * mm});
            skLineSegment(sketch, "E129.0.2", {"start": v(-320.26, -255.4) * mm, "end": v(0, -409.63) * mm});
            skLineSegment(sketch, "E129.0.3", {"start": v(0, -409.63) * mm, "end": v(320.26, -255.4) * mm});
            skLineSegment(sketch, "E129.0.4", {"start": v(320.26, -255.4) * mm, "end": v(399.36, 91.15) * mm});
            skLineSegment(sketch, "E129.0.5", {"start": v(399.36, 91.15) * mm, "end": v(177.73, 369.06) * mm});
            skLineSegment(sketch, "E129.0.6", {"start": v(177.73, 369.06) * mm, "end": v(-177.73, 369.06) * mm});
            skLineSegment(sketch, "E130", {"start": v(0, 369.06) * mm, "end": v(0, 343.66) * mm});
            skCircle(sketch, "E131.cCircle", {"center": v(0, 0) * mm, "radius": 343.66 * mm, "construction": true});
            skLineSegment(sketch, "E131.0", {"start": v(-165.5, 343.66) * mm, "end": v(165.5, 343.66) * mm});
            skLineSegment(sketch, "E131.1", {"start": v(165.5, 343.66) * mm, "end": v(371.87, 84.88) * mm});
            skLineSegment(sketch, "E131.2", {"start": v(371.87, 84.88) * mm, "end": v(298.22, -237.82) * mm});
            skLineSegment(sketch, "E131.3", {"start": v(298.22, -237.82) * mm, "end": v(0, -381.44) * mm});
            skLineSegment(sketch, "E131.4", {"start": v(0, -381.44) * mm, "end": v(-298.22, -237.82) * mm});
            skLineSegment(sketch, "E131.5", {"start": v(-298.22, -237.82) * mm, "end": v(-371.87, 84.88) * mm});
            skLineSegment(sketch, "E131.6", {"start": v(-371.87, 84.88) * mm, "end": v(-165.5, 343.66) * mm});
            skPoint(sketch, "E131.0.midPoint", {"position": v(0, 343.66) * mm});
            skSolve(sketch);
        }
        {
            var Q0;
            {var subQ7=sQuery(id+"F36.wireOp",EDGE,"E129.0.0");Q0=makeQuery(id+"F36.imprint","IMPRINT",FACE,{"disambiguationData":[TD([[makeQuery(id+"F36.imprint","IMPRINT",EDGE,{"derivedFrom":subQ7}),-1.0]])]});}
            extrude(context, id + "F37", {"entities" : qUnion([Q0]), "operationType" : NewBodyOperationType.ADD, "depth" : 330.2 * mm, "offsetDistance" : 25.4 * mm});
        }
        {
            var Q0;
            Q0=makeQuery(id+"F37.opExtrude","CAP_FACE",FACE,{"disambiguationData":[OSD([sQuery(id+"F36.wireOp",EDGE,"E129.0.0"),sQuery(id+"F36.wireOp",EDGE,"E129.0.1"),sQuery(id+"F36.wireOp",EDGE,"E129.0.2"),sQuery(id+"F36.wireOp",EDGE,"E129.0.3"),sQuery(id+"F36.wireOp",EDGE,"E129.0.4"),sQuery(id+"F36.wireOp",EDGE,"E129.0.5"),sQuery(id+"F36.wireOp",EDGE,"E129.0.6"),sQuery(id+"F36.wireOp",EDGE,"E131.0"),sQuery(id+"F36.wireOp",EDGE,"E131.1"),sQuery(id+"F36.wireOp",EDGE,"E131.2"),sQuery(id+"F36.wireOp",EDGE,"E131.3"),sQuery(id+"F36.wireOp",EDGE,"E131.4"),sQuery(id+"F36.wireOp",EDGE,"E131.5"),sQuery(id+"F36.wireOp",EDGE,"E131.6")])],"isStart":false});
            var sketch = newSketch(context, id + "F38", { "sketchPlane" : qUnion([Q0])});
            skLineSegment(sketch, "E132.0", {"start": v(-177.73, 369.06) * mm, "end": v(177.73, 369.06) * mm});
            skLineSegment(sketch, "E133.0", {"start": v(-399.36, 91.15) * mm, "end": v(-177.73, 369.06) * mm});
            skLineSegment(sketch, "E134.0", {"start": v(-320.26, -255.4) * mm, "end": v(-399.36, 91.15) * mm});
            skLineSegment(sketch, "E135.0", {"start": v(0, -409.63) * mm, "end": v(-320.26, -255.4) * mm});
            skLineSegment(sketch, "E136.0", {"start": v(320.26, -255.4) * mm, "end": v(0, -409.63) * mm});
            skLineSegment(sketch, "E137.0", {"start": v(399.36, 91.15) * mm, "end": v(320.26, -255.4) * mm});
            skLineSegment(sketch, "E138.0", {"start": v(177.73, 369.06) * mm, "end": v(399.36, 91.15) * mm});
            skSolve(sketch);
        }
        {
            var Q0;
            Q0=makeQuery(id+"F38.imprint","IMPRINT",FACE,{"disambiguationData":[TD([[makeQuery(id+"F38.imprint","IMPRINT",EDGE,{"derivedFrom":sQuery(id+"F38.wireOp",EDGE,"E132.0")}),-1.0]])]});
            var Q1;
            Q1=makeQuery(id+"F38.imprint","IMPRINT",FACE,{"disambiguationData":[TD([[makeQuery(id+"F38.imprint","IMPRINT",EDGE,{"derivedFrom":makeQuery(id+"F37.opExtrude","CAP_EDGE",EDGE,{"disambiguationData":[OSD([sQuery(id+"F36.wireOp",EDGE,"E131.0")])],"isStart":false})}),-1.0]])]});
            extrude(context, id + "F39", {"entities" : qUnion([Q0, Q1]), "operationType" : NewBodyOperationType.ADD, "depth" : 25.4 * mm, "offsetDistance" : 25.4 * mm});
        }
        {
            var Q0;
            Q0=makeQuery(id+"F39.boolean.opBoolean","MERGE",FACE,{"derivedFrom":[makeQuery(id+"F37.boolean.opBoolean","MERGE",FACE,{"derivedFrom":[makeQuery(id+"F35.opExtrude","SWEPT_FACE",FACE,{"disambiguationData":[OSD([sQuery(id+"F14.wireOp",EDGE,"E97.0")])]}),makeQuery(id+"F37.opExtrude","SWEPT_FACE",FACE,{"disambiguationData":[OSD([sQuery(id+"F36.wireOp",EDGE,"E129.0.6")])]})]}),makeQuery(id+"F39.opExtrude","SWEPT_FACE",FACE,{"disambiguationData":[OSD([sQuery(id+"F38.wireOp",EDGE,"E132.0")])]})]});
            var sketch = newSketch(context, id + "F40", { "sketchPlane" : qUnion([Q0])});
            skLineSegment(sketch, "E139.0.0", {"start": v(177.73, -254) * mm, "end": v(-177.73, -254) * mm});
            skLineSegment(sketch, "E139.0.1", {"start": v(-177.73, -254) * mm, "end": v(-177.73, -635) * mm});
            skLineSegment(sketch, "E139.0.2", {"start": v(-177.73, -635) * mm, "end": v(177.73, -635) * mm});
            skLineSegment(sketch, "E139.0.3", {"start": v(177.73, -635) * mm, "end": v(177.73, -254) * mm});
            skLineSegment(sketch, "E140", {"start": v(0, -254) * mm, "end": v(0, -279.4) * mm});
            skLineSegment(sketch, "E141", {"start": v(-177.73, -444.5) * mm, "end": v(-152.33, -444.5) * mm});
            skLineSegment(sketch, "E142", {"start": v(-152.33, -444.5) * mm, "end": v(0, -444.5) * mm});
            skLineSegment(sketch, "E143", {"start": v(0, -279.4) * mm, "end": v(0, -444.5) * mm});
            skLineSegment(sketch, "E144.bottom", {"start": v(-152.33, -279.4) * mm, "end": v(152.33, -279.4) * mm});
            skLineSegment(sketch, "E144.top", {"start": v(-152.33, -609.6) * mm, "end": v(152.33, -609.6) * mm});
            skLineSegment(sketch, "E144.left", {"start": v(-152.33, -279.4) * mm, "end": v(-152.33, -609.6) * mm});
            skLineSegment(sketch, "E144.right", {"start": v(152.33, -279.4) * mm, "end": v(152.33, -609.6) * mm});
            skPoint(sketch, "E144.middle", {"position": v(0, -444.5) * mm});
            skSolve(sketch);
        }
        {
            var Q0;
            {var subQ4=sQuery(id+"F40.wireOp",EDGE,"E142");Q0=makeQuery(id+"F40.imprint","IMPRINT",FACE,{"disambiguationData":[TD([[makeQuery(id+"F40.imprint","IMPRINT",EDGE,{"derivedFrom":subQ4}),-1.0]])]});}
            var Q1;
            {var subQ0=sQuery(id+"F40.wireOp",EDGE,"E142");Q1=makeQuery(id+"F40.imprint","IMPRINT",FACE,{"disambiguationData":[TD([[makeQuery(id+"F40.imprint","IMPRINT",EDGE,{"derivedFrom":subQ0}),1.0]])]});}
            extrude(context, id + "F41", {"entities" : qUnion([Q0, Q1]), "operationType" : NewBodyOperationType.REMOVE, "oppositeDirection" : true, "depth" : 25.4 * mm, "offsetDistance" : 25.4 * mm});
        }
        {
            var Q0;
            {var subQ1=sQuery(id+"F40.wireOp",EDGE,"E140");Q0=makeQuery(id+"F40.imprint","IMPRINT",FACE,{"disambiguationData":[TD([[makeQuery(id+"F40.imprint","IMPRINT",EDGE,{"derivedFrom":subQ1}),-1.0]])]});}
            var Q1;
            {var subQ0=sQuery(id+"F40.wireOp",EDGE,"E142");Q1=makeQuery(id+"F40.imprint","IMPRINT",FACE,{"disambiguationData":[TD([[makeQuery(id+"F40.imprint","IMPRINT",EDGE,{"derivedFrom":subQ0}),1.0]])]});}
            var Q2;
            {var subQ4=sQuery(id+"F40.wireOp",EDGE,"E142");Q2=makeQuery(id+"F40.imprint","IMPRINT",FACE,{"disambiguationData":[TD([[makeQuery(id+"F40.imprint","IMPRINT",EDGE,{"derivedFrom":subQ4}),-1.0]])]});}
            var Q3;
            {var subQ1=sQuery(id+"F40.wireOp",EDGE,"E139.0.2");Q3=makeQuery(id+"F40.imprint","IMPRINT",FACE,{"disambiguationData":[TD([[makeQuery(id+"F40.imprint","IMPRINT",EDGE,{"derivedFrom":subQ1}),1.0]])]});}
            extrude(context, id + "F42", {"entities" : qUnion([Q0, Q1, Q2, Q3]), "depth" : 12.7 * mm, "offsetDistance" : 25.4 * mm});
        }
    });
